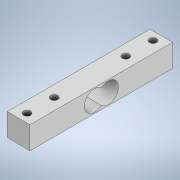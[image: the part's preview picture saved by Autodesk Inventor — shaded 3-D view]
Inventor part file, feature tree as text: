
AUTODESK INVENTOR PART (.ipt)
format: ipt  version: 2020 (Build 240168000, 168)  size: 133,632 bytes
history: native  units: in
note: dims shown in document units (in); Inventor stores cm internally (conversion verified against a paired STEP export)
features: extrude x3, sketch x3
ambient origin geometry x8: Origin, YZ Plane, XZ Plane, XY Plane, X Axis, Y Axis, Z Axis, Center Point
bodies: Solid1 (feature_tree)
feature tree (6):
  extrude  "Extrusion1"  Depth=0.5in
  extrude  "Extrusion2"  Depth=3.15in
  extrude  "Extrusion3"  Depth=0.25in
  sketch  "Sketch1"  dims[d0=0.5in d1=0.5in]
  sketch  "Sketch2"  dims[d2=3.15in d3=0.0in d4=0.45in]
  sketch  "Sketch3"  dims[d5=0.45in d6=0.25in d7=0.3in d8=1.575in d9=0.0in d10=0.0in d11=0.1575in d12=0.185in d13=0.25in d14=0.1575in d15=0.6in d16=0.25in d17=0.1575in d18=0.1575in d19=0.25in d20=0.25in d21=0.185in d22=0.6in d23=0.0in d24=0.0in]
